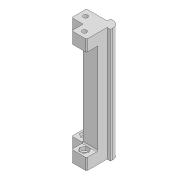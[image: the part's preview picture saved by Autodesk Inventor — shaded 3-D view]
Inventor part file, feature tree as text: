
AUTODESK INVENTOR PART (.ipt)
format: ipt  version: 2020 (Build 240168000, 168)  size: 231,936 bytes
history: native  units: mm
features: extrude x7, sketch x7, other x3, fillet x1
ambient origin geometry x8: Origin, YZ Plane, XZ Plane, XY Plane, X Axis, Y Axis, Z Axis, Center Point
bodies: Body1 (feature_tree)
feature tree (18):
  other  "Sólido1"
  extrude  "Extrusão1"  Depth=16.0mm
  extrude  "Extrusão2"  Depth=3.0mm
  extrude  "Extrusão3"  Depth=3.0mm
  extrude  "Extrusão4"  Depth=5.2mm
  extrude  "Extrusão5"  Depth=8.0mm
  fillet  "Arredondamento1"  Radius=100.0mm
  extrude  "Extrusão6"  Depth=10.0mm
  extrude  "Extrusão7"  TaperAngle=0.0deg  [1 undecoded]
  sketch  "Esboço1"  dims[d0=16.0mm d1=16.0mm]
  sketch  "Esboço2"  dims[d2=8.0mm d3=3.0mm]
  sketch  "Esboço3"  dims[d4=8.0mm d5=3.0mm]
  sketch  "Esboço4"  dims[d6=6.0mm d7=5.2mm]
  sketch  "Esboço5"  dims[d8=8.0mm d9=8.0mm d10=100.0mm d11=0.0mm]
  sketch  "Esboço6"  dims[d12=10.0mm d13=10.0mm]
  sketch  "Esboço7"  dims[d14=10.0mm d15=0.0mm d16=0.0mm d17=4.0mm d18=5.0mm d19=200.0mm d20=0.0mm d21=10.0mm d22=10.0mm d23=0.0mm d24=4.0mm d25=5.0mm d26=7.0mm d27=6.0mm d28=200.0mm d29=0.0mm d30=1.0mm d31=13.0mm d32=6.8mm d33=6.8mm d34=3.0mm d35=0.0mm d36=3.0mm d37=0.0mm d38=0.0mm]
  other  "Contorno projetado1"
  other  "Contorno projetado2"
note: 1 required parameter value undecoded (feature->parameter linkage not recoverable at this tier; creation-order binding heuristic only, values carry confidence <= 0.55)
